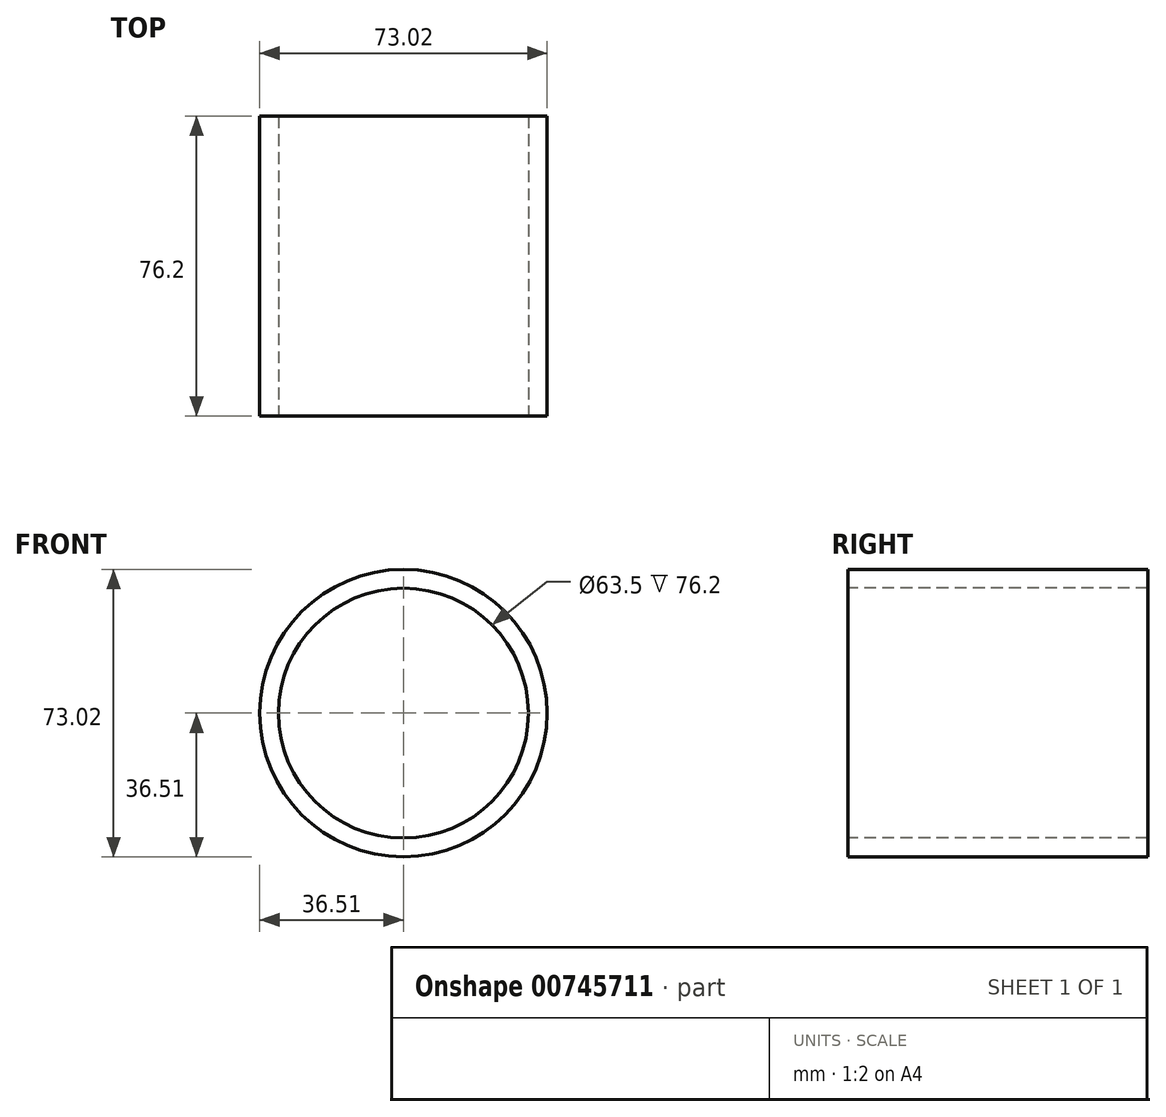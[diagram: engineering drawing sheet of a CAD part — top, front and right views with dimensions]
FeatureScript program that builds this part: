
annotation { "Feature Type Name" : "Feature", "Feature Type Description" : "" }
export const myFeature = defineFeature(function(context is Context, id is Id, definition is map)
    precondition{}
    {
        {
            var Q0;
            Q0=qCreatedBy(makeId("Front.planeOp"),FACE);
            var sketch = newSketch(context, id + "F0", { "sketchPlane" : qUnion([Q0])});
            skCircle(sketch, "E0", {"center": v(0, 0) * mm, "radius": 31.75 * mm});
            skCircle(sketch, "E1", {"center": v(0, 0) * mm, "radius": 36.51 * mm});
            skSolve(sketch);
        }
        {
            var Q0;
            Q0=makeQuery(id+"F0.imprint","IMPRINT",FACE,{"disambiguationData":[TD([[makeQuery(id+"F0.imprint","IMPRINT",EDGE,{"derivedFrom":sQuery(id+"F0.wireOp",EDGE,"E0")}),-1.0]])]});
            extrude(context, id + "F1", {"entities" : qUnion([Q0]), "oppositeDirection" : true, "depth" : 76.2 * mm, "offsetDistance" : 25.4 * mm});
        }
    });
